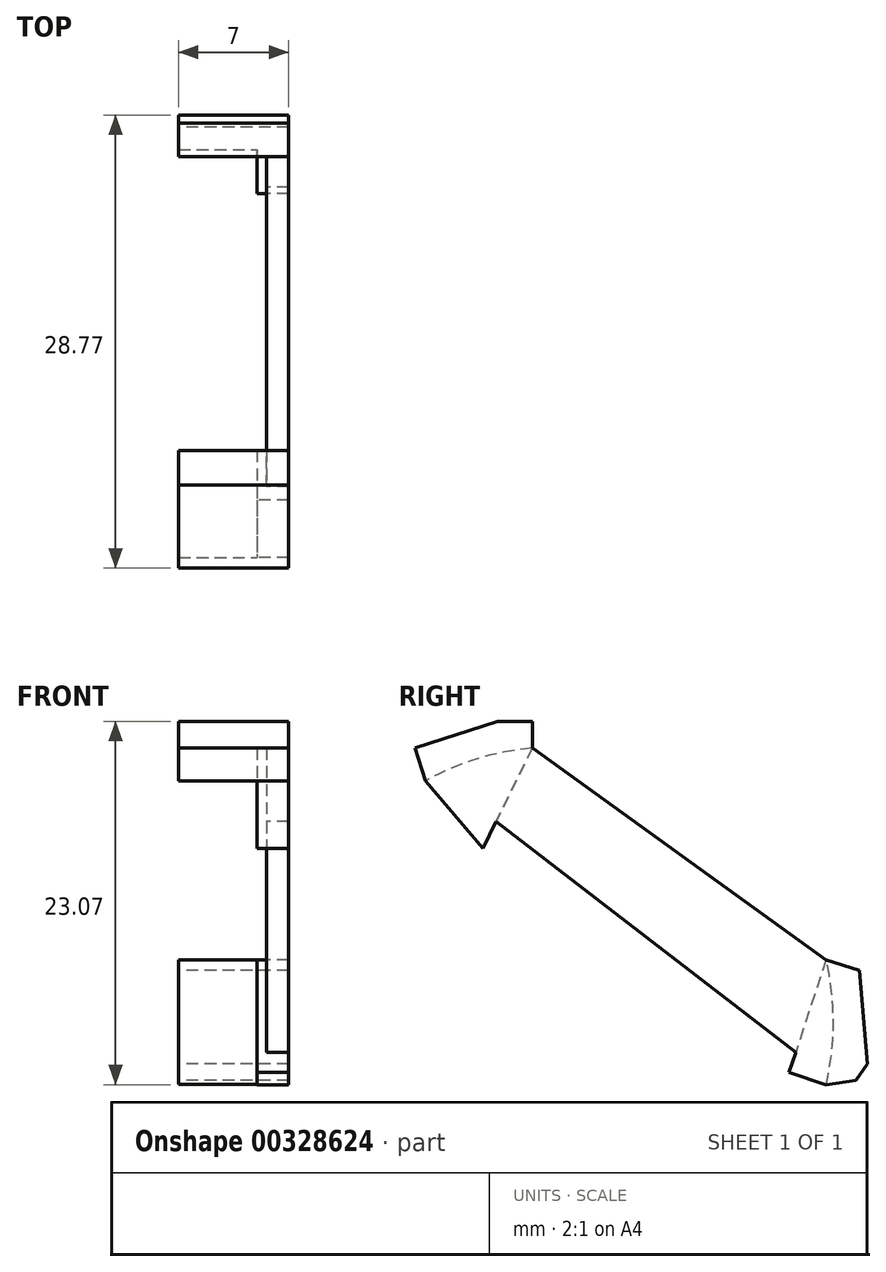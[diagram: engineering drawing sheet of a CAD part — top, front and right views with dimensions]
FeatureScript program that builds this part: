
annotation { "Feature Type Name" : "Feature", "Feature Type Description" : "" }
export const myFeature = defineFeature(function(context is Context, id is Id, definition is map)
    precondition{}
    {
        {
            var Q0;
            Q0=qCreatedBy(makeId("Right.planeOp"),FACE);
            var sketch = newSketch(context, id + "F0", { "sketchPlane" : qUnion([Q0])});
            skCircle(sketch, "E0", {"center": v(-45.41, 29.5) * mm, "radius": 17.5 * mm});
            skLineSegment(sketch, "E1", {"start": v(-47.03, 46.92) * mm, "end": v(-28.37, 33.48) * mm});
            skLineSegment(sketch, "E2", {"start": v(-47.03, 46.92) * mm, "end": v(-50.17, 40.55) * mm});
            skLineSegment(sketch, "E3", {"start": v(-50.17, 40.55) * mm, "end": v(-53.83, 44.84) * mm});
            skLineSegment(sketch, "E4", {"start": v(-28.37, 33.48) * mm, "end": v(-30.72, 26.31) * mm});
            skLineSegment(sketch, "E5", {"start": v(-30.72, 26.31) * mm, "end": v(-28.37, 25.54) * mm});
            skLineSegment(sketch, "E6", {"start": v(-49.33, 42.25) * mm, "end": v(-30.3, 27.6) * mm});
            skLineSegment(sketch, "E7", {"start": v(-28.37, 33.48) * mm, "end": v(-26.25, 32.78) * mm});
            skLineSegment(sketch, "E8", {"start": v(-26.25, 32.78) * mm, "end": v(-25.73, 26.85) * mm});
            skLineSegment(sketch, "E9", {"start": v(-25.73, 26.85) * mm, "end": v(-26.49, 25.81) * mm});
            skLineSegment(sketch, "E10", {"start": v(-26.49, 25.81) * mm, "end": v(-28.37, 25.54) * mm});
            skLineSegment(sketch, "E11", {"start": v(-53.83, 44.84) * mm, "end": v(-54.5, 46.92) * mm});
            skLineSegment(sketch, "E12", {"start": v(-54.5, 46.92) * mm, "end": v(-49.24, 48.61) * mm});
            skLineSegment(sketch, "E13", {"start": v(-49.24, 48.61) * mm, "end": v(-47.03, 48.61) * mm});
            skLineSegment(sketch, "E14", {"start": v(-47.03, 48.61) * mm, "end": v(-47.03, 46.92) * mm});
            skSolve(sketch);
        }
        {
            var Q0;
            {var subQ3=sQuery(id+"F0.wireOp",EDGE,"E3");Q0=makeQuery(id+"F0.imprint","IMPRINT",FACE,{"disambiguationData":[TD([[makeQuery(id+"F0.imprint","IMPRINT",EDGE,{"derivedFrom":subQ3}),-1.0]])]});}
            var Q1;
            {var subQ0=sQuery(id+"F0.wireOp",EDGE,"E1");Q1=makeQuery(id+"F0.imprint","IMPRINT",FACE,{"disambiguationData":[TD([[makeQuery(id+"F0.imprint","IMPRINT",EDGE,{"derivedFrom":subQ0}),-1.0]])]});}
            var Q2;
            {var subQ0=sQuery(id+"F0.wireOp",EDGE,"E5");Q2=makeQuery(id+"F0.imprint","IMPRINT",FACE,{"disambiguationData":[TD([[makeQuery(id+"F0.imprint","IMPRINT",EDGE,{"derivedFrom":subQ0}),1.0]])]});}
            var Q3;
            {var subQ1=sQuery(id+"F0.wireOp",EDGE,"E7");Q3=makeQuery(id+"F0.imprint","IMPRINT",FACE,{"disambiguationData":[TD([[makeQuery(id+"F0.imprint","IMPRINT",EDGE,{"derivedFrom":subQ1}),-1.0]])]});}
            var Q4;
            {var subQ0=sQuery(id+"F0.wireOp",EDGE,"E11");Q4=makeQuery(id+"F0.imprint","IMPRINT",FACE,{"disambiguationData":[TD([[makeQuery(id+"F0.imprint","IMPRINT",EDGE,{"derivedFrom":subQ0}),-1.0]])]});}
            extrude(context, id + "F1", {"entities" : qUnion([Q0, Q1, Q2, Q3, Q4]), "depth" : 2 * mm});
        }
        {
            var Q0;
            {var subQ0=sQuery(id+"F0.wireOp",EDGE,"E1");Q0=makeQuery(id+"F0.imprint","IMPRINT",FACE,{"disambiguationData":[TD([[makeQuery(id+"F0.imprint","IMPRINT",EDGE,{"derivedFrom":subQ0}),-1.0]])]});}
            extrude(context, id + "F2", {"entities" : qUnion([Q0]), "operationType" : NewBodyOperationType.REMOVE, "depth" : 0.6 * mm});
        }
        {
            var Q0;
            {var subQ0=sQuery(id+"F0.wireOp",EDGE,"E11");Q0=makeQuery(id+"F0.imprint","IMPRINT",FACE,{"disambiguationData":[TD([[makeQuery(id+"F0.imprint","IMPRINT",EDGE,{"derivedFrom":subQ0}),-1.0]])]});}
            var Q1;
            {var subQ1=sQuery(id+"F0.wireOp",EDGE,"E7");Q1=makeQuery(id+"F0.imprint","IMPRINT",FACE,{"disambiguationData":[TD([[makeQuery(id+"F0.imprint","IMPRINT",EDGE,{"derivedFrom":subQ1}),-1.0]])]});}
            extrude(context, id + "F3", {"entities" : qUnion([Q0, Q1]), "operationType" : NewBodyOperationType.ADD, "oppositeDirection" : true, "depth" : 5 * mm});
        }
    });
